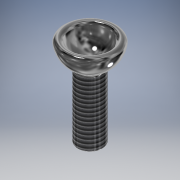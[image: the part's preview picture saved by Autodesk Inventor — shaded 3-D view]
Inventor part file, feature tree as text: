
AUTODESK INVENTOR PART (.ipt)
format: ipt  version: 2018 (Build 220112000, 112)  size: 176,128 bytes
history: native  units: mm
features: fillet x2, sketch x2, revolve x1, extrude x1, thread x1
ambient origin geometry x8: Origin, YZ Plane, XZ Plane, XY Plane, X Axis, Y Axis, Z Axis, Center Point
bodies: Solid1 (feature_tree)
feature tree (7):
  revolve  "Revolution1"  [1 undecoded]
  extrude  "Extrusion1"  Depth=3.5mm
  fillet  "Fillet1"  Radius=0.5mm
  fillet  "Fillet2"  [1 undecoded]
  thread  "Thread2"  [1 undecoded]
  sketch  "Sketch1"  dims[d0=11.75mm d1=1.625mm]
  sketch  "Sketch2"  dims[d2=2.5mm d3=3.5mm d4=0.5mm d5=90.0deg d6=2.0mm d7=1.5mm d8=0.0mm d9=0.2mm d10=0.5mm d13=8.161mm d14=0.0mm]
note: 3 required parameter values undecoded (feature->parameter linkage not recoverable at this tier; creation-order binding heuristic only, values carry confidence <= 0.55)